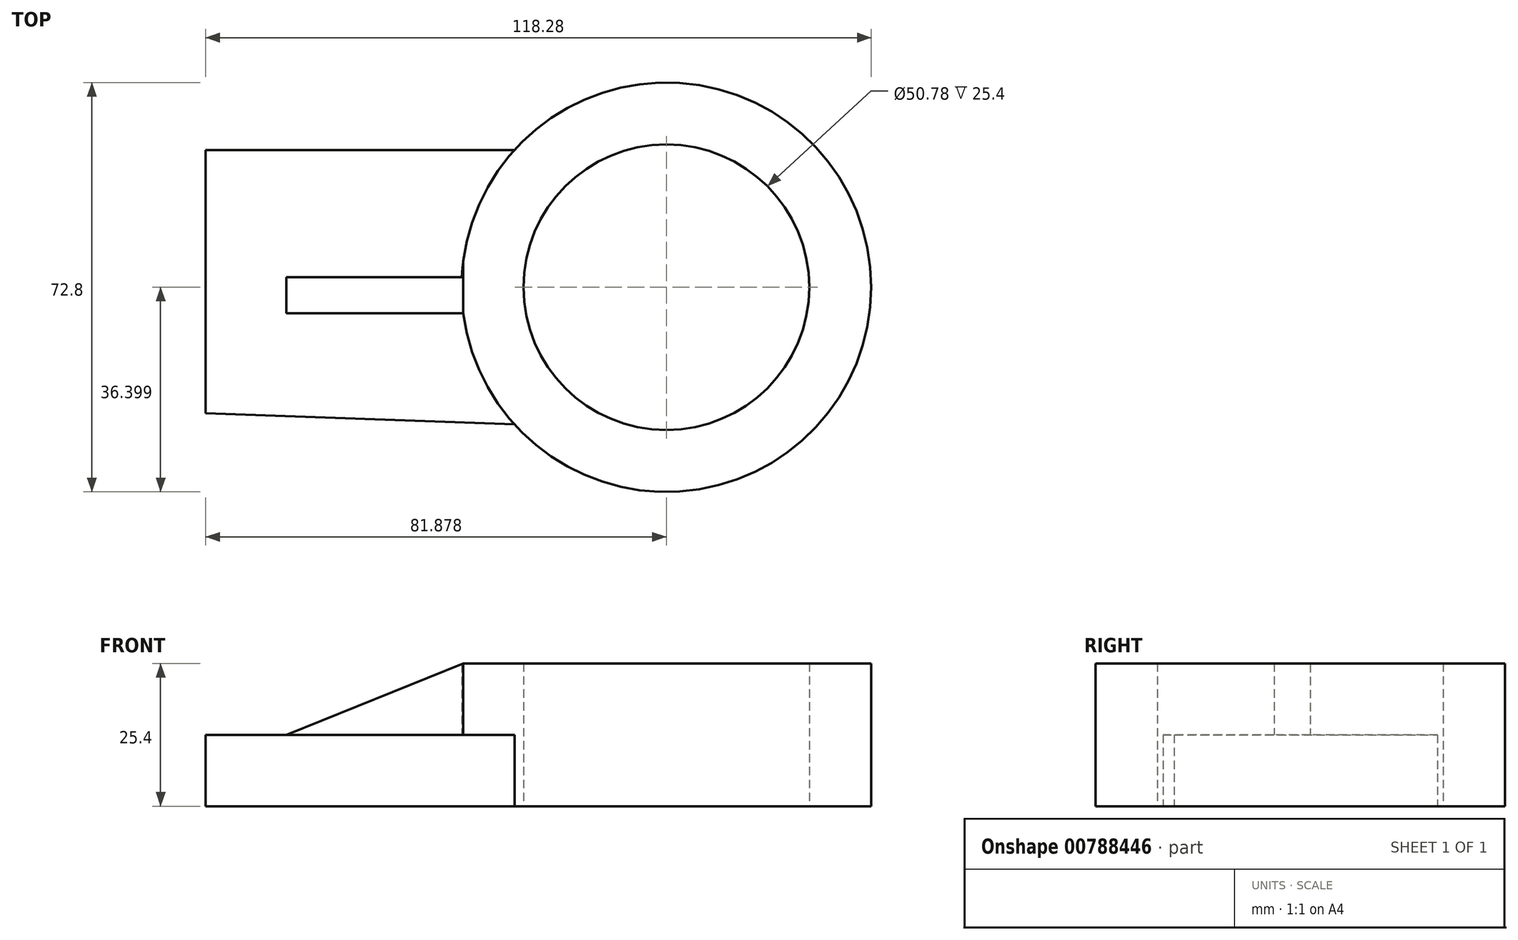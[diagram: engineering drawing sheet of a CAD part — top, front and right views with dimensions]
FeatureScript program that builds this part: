
annotation { "Feature Type Name" : "Feature", "Feature Type Description" : "" }
export const myFeature = defineFeature(function(context is Context, id is Id, definition is map)
    precondition{}
    {
        {
            var Q0;
            Q0=qCreatedBy(makeId("Top.planeOp"),FACE);
            var sketch = newSketch(context, id + "F0", { "sketchPlane" : qUnion([Q0])});
            skArc(sketch, "E0", {"start": v(0.25, -14.28) * mm, "mid": v(72.73, -8.19) * mm, "end": v(0, -7.86) * mm});
            skCircle(sketch, "E1", {"center": v(36.36, -9.63) * mm, "radius": 25.39 * mm});
            skLineSegment(sketch, "E2", {"start": v(9.36, 14.78) * mm, "end": v(-45.52, 14.78) * mm});
            skLineSegment(sketch, "E3", {"start": v(9.36, -34.04) * mm, "end": v(-45.52, -32.02) * mm});
            skLineSegment(sketch, "E4", {"start": v(-45.52, -32.02) * mm, "end": v(-45.52, 14.78) * mm});
            skLineSegment(sketch, "E5", {"start": v(0, -7.86) * mm, "end": v(-31.2, -7.86) * mm});
            skLineSegment(sketch, "E6", {"start": v(-31.2, -7.86) * mm, "end": v(-31.2, -14.28) * mm});
            skLineSegment(sketch, "E7", {"start": v(-31.2, -14.28) * mm, "end": v(0.25, -14.28) * mm});
            skSolve(sketch);
        }
        {
            var Q0;
            Q0=makeQuery(id+"F0.imprint","IMPRINT",FACE,{"disambiguationData":[TD([[makeQuery(id+"F0.imprint","IMPRINT",EDGE,{"derivedFrom":sQuery(id+"F0.wireOp",EDGE,"E1")}),-1.0]])]});
            extrude(context, id + "F1", {"entities" : qUnion([Q0]), "depth" : 25.4 * mm, "offsetDistance" : 25.4 * mm});
        }
        {
            var Q0;
            {var subQ0=sQuery(id+"F0.wireOp",EDGE,"E2");Q0=makeQuery(id+"F0.imprint","IMPRINT",FACE,{"disambiguationData":[TD([[makeQuery(id+"F0.imprint","IMPRINT",EDGE,{"derivedFrom":subQ0}),1.0]])]});}
            extrude(context, id + "F2", {"entities" : qUnion([Q0]), "operationType" : NewBodyOperationType.ADD, "depth" : 12.7 * mm, "offsetDistance" : 25.4 * mm});
        }
        {
            var Q0;
            Q0=makeQuery(id+"F1.opExtrude","SWEPT_FACE",FACE,{"disambiguationData":[OSD([sQuery(id+"F0.wireOp",EDGE,"E7")])]});
            var sketch = newSketch(context, id + "F3", { "sketchPlane" : qUnion([Q0])});
            skLineSegment(sketch, "E8", {"start": v(0.25, 25.4) * mm, "end": v(-31.2, 12.7) * mm});
            skSolve(sketch);
        }
        {
            var Q0;
            Q0=makeQuery(id+"F3.imprint","IMPRINT",FACE,{"disambiguationData":[TD([[makeQuery(id+"F3.imprint","IMPRINT",EDGE,{"derivedFrom":sQuery(id+"F3.wireOp",EDGE,"E8")}),-1.0]])]});
            extrude(context, id + "F4", {"entities" : qUnion([Q0]), "operationType" : NewBodyOperationType.REMOVE, "oppositeDirection" : true, "depth" : 25.4 * mm, "offsetDistance" : 25.4 * mm});
        }
    });
